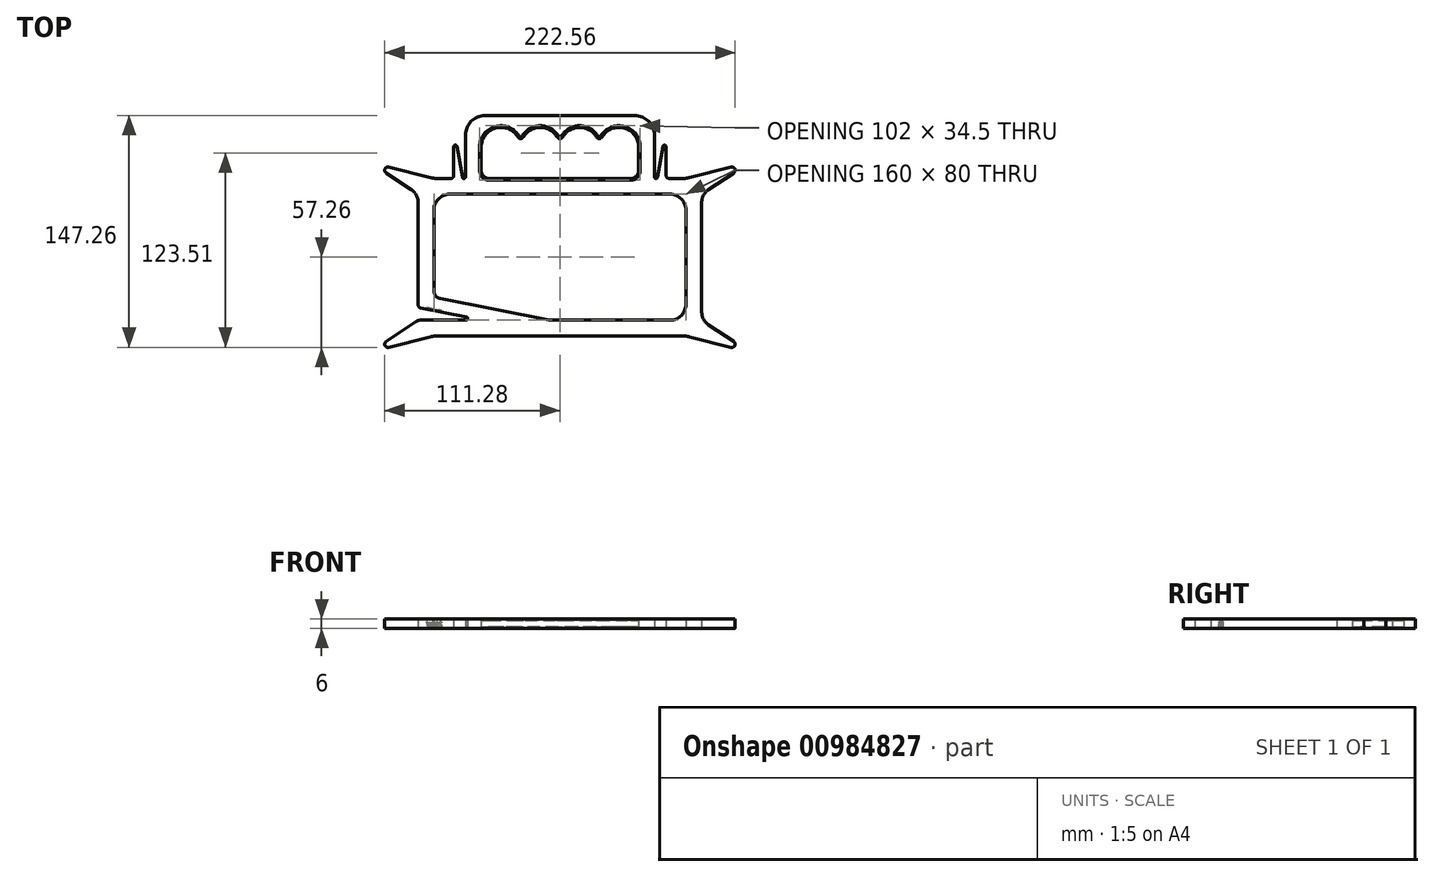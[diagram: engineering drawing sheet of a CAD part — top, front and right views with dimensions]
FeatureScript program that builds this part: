
annotation { "Feature Type Name" : "Feature", "Feature Type Description" : "" }
export const myFeature = defineFeature(function(context is Context, id is Id, definition is map)
    precondition{}
    {
        {
            var Q0;
            Q0=qCreatedBy(makeId("Top.planeOp"),FACE);
            var sketch = newSketch(context, id + "F0", { "sketchPlane" : qUnion([Q0])});
            skLineSegment(sketch, "E0.top", {"start": v(-77.54, -50) * mm, "end": v(77.54, -50) * mm});
            skLineSegment(sketch, "E0.left", {"start": v(-90, 34.65) * mm, "end": v(-90, -30.34) * mm});
            skLineSegment(sketch, "E0.right", {"start": v(90, 34.65) * mm, "end": v(90, -34.65) * mm});
            skLineSegment(sketch, "E1.bottom", {"start": v(70, 40) * mm, "end": v(-70, 40) * mm});
            skLineSegment(sketch, "E1.top", {"start": v(-59.6, -40) * mm, "end": v(-68.78, -40) * mm});
            skLineSegment(sketch, "E1.left", {"start": v(80, 30) * mm, "end": v(80, -30) * mm});
            skLineSegment(sketch, "E1.right", {"start": v(-80, 30) * mm, "end": v(-80, -21.4) * mm});
            skPoint(sketch, "E1.middle", {"position": v(0, 0) * mm});
            skLineSegment(sketch, "E2.top", {"start": v(47.5, 90) * mm, "end": v(-47.5, 90) * mm});
            skLineSegment(sketch, "E2.right", {"start": v(-60, 51) * mm, "end": v(-60, 77.5) * mm});
            skPoint(sketch, "E2.middle", {"position": v(0, 70) * mm});
            skLineSegment(sketch, "E3.top", {"start": v(45, 50) * mm, "end": v(-45, 50) * mm});
            skLineSegment(sketch, "E3.left", {"start": v(50, 70) * mm, "end": v(50, 55) * mm});
            skLineSegment(sketch, "E3.right", {"start": v(-50, 70) * mm, "end": v(-50, 55) * mm});
            skPoint(sketch, "E3.middle", {"position": v(0, 60) * mm});
            skArc(sketch, "E4", {"start": v(-26.72, 76.33) * mm, "mid": v(-40.78, 82.06) * mm, "end": v(-50, 70) * mm});
            skArc(sketch, "E5.1.0.0", {"start": v(-1.72, 76.33) * mm, "mid": v(-12.5, 82.5) * mm, "end": v(-23.28, 76.33) * mm});
            skArc(sketch, "E5.2.0.0", {"start": v(23.28, 76.33) * mm, "mid": v(12.5, 82.5) * mm, "end": v(1.72, 76.33) * mm});
            skArc(sketch, "E5.3.0.0", {"start": v(50, 70) * mm, "mid": v(40.78, 82.06) * mm, "end": v(26.72, 76.33) * mm});
            skPoint(sketch, "E6.visualSharp", {"position": v(-25, 70) * mm});
            skArc(sketch, "E6.filletArc", {"start": v(-26.72, 76.33) * mm, "mid": v(-25, 75.35) * mm, "end": v(-23.28, 76.33) * mm});
            skArc(sketch, "E7.filletArc", {"start": v(-1.72, 76.33) * mm, "mid": v(0, 75.35) * mm, "end": v(1.72, 76.33) * mm});
            skPoint(sketch, "E8.visualSharp", {"position": v(25, 70) * mm});
            skArc(sketch, "E8.filletArc", {"start": v(23.28, 76.33) * mm, "mid": v(25, 75.35) * mm, "end": v(26.72, 76.33) * mm});
            skPoint(sketch, "E9.visualSharp", {"position": v(-60, 90) * mm});
            skArc(sketch, "E9.filletArc", {"start": v(-47.5, 90) * mm, "mid": v(-56.34, 86.34) * mm, "end": v(-60, 77.5) * mm});
            skPoint(sketch, "E10.visualSharp", {"position": v(60, 90) * mm});
            skArc(sketch, "E10.filletArc", {"start": v(60, 77.5) * mm, "mid": v(56.34, 86.34) * mm, "end": v(47.5, 90) * mm});
            skPoint(sketch, "E11.visualSharp", {"position": v(-50, 50) * mm});
            skArc(sketch, "E11.filletArc", {"start": v(-50, 55) * mm, "mid": v(-48.54, 51.46) * mm, "end": v(-45, 50) * mm});
            skPoint(sketch, "E12.visualSharp", {"position": v(50, 50) * mm});
            skArc(sketch, "E12.filletArc", {"start": v(45, 50) * mm, "mid": v(48.54, 51.46) * mm, "end": v(50, 55) * mm});
            skPoint(sketch, "E13.visualSharp", {"position": v(-60, 50) * mm});
            skPoint(sketch, "E14.visualSharp", {"position": v(-80, 40) * mm});
            skPoint(sketch, "E15.visualSharp", {"position": v(-80, -40) * mm});
            skPoint(sketch, "E16.visualSharp", {"position": v(80, -40) * mm});
            skPoint(sketch, "E17.visualSharp", {"position": v(80, 40) * mm});
            skLineSegment(sketch, "E18", {"start": v(94.45, 42.97) * mm, "end": v(110.4, 53.6) * mm});
            skLineSegment(sketch, "E19", {"start": v(82.39, 50.6) * mm, "end": v(108.8, 57.2) * mm});
            skPoint(sketch, "E20.visualSharp", {"position": v(120, 60) * mm});
            skArc(sketch, "E20.filletArc", {"start": v(110.4, 53.6) * mm, "mid": v(111.11, 56.07) * mm, "end": v(108.8, 57.2) * mm});
            skLineSegment(sketch, "E21.MirrorCS", {"start": v(-82.39, 50.6) * mm, "end": v(-108.8, 57.2) * mm});
            skLineSegment(sketch, "E22.MirrorCS", {"start": v(-94.45, 42.97) * mm, "end": v(-110.4, 53.6) * mm});
            skArc(sketch, "E23.MirrorCS", {"start": v(-110.4, 53.6) * mm, "mid": v(-111.11, 56.07) * mm, "end": v(-108.8, 57.2) * mm});
            skLineSegment(sketch, "E24.MirrorCS", {"start": v(-82.39, -50.6) * mm, "end": v(-108.8, -57.2) * mm});
            skArc(sketch, "E25.MirrorCS", {"start": v(-110.4, -53.6) * mm, "mid": v(-111.11, -56.07) * mm, "end": v(-108.8, -57.2) * mm});
            skLineSegment(sketch, "E26.MirrorCS", {"start": v(-91.26, -40.84) * mm, "end": v(-110.4, -53.6) * mm});
            skLineSegment(sketch, "E27.MirrorCS", {"start": v(82.39, -50.6) * mm, "end": v(108.8, -57.2) * mm});
            skLineSegment(sketch, "E28.MirrorCS", {"start": v(94.45, -42.97) * mm, "end": v(110.4, -53.6) * mm});
            skArc(sketch, "E29.MirrorCS", {"start": v(110.4, -53.6) * mm, "mid": v(111.11, -56.07) * mm, "end": v(108.8, -57.2) * mm});
            skPoint(sketch, "E30.visualSharp", {"position": v(90, 40) * mm});
            skArc(sketch, "E30.filletArc", {"start": v(94.45, 42.97) * mm, "mid": v(91.18, 39.37) * mm, "end": v(90, 34.65) * mm});
            skPoint(sketch, "E31.visualSharp", {"position": v(90, -40) * mm});
            skArc(sketch, "E31.filletArc", {"start": v(90, -34.65) * mm, "mid": v(91.18, -39.37) * mm, "end": v(94.45, -42.97) * mm});
            skPoint(sketch, "E32.visualSharp", {"position": v(-90, -40) * mm});
            skPoint(sketch, "E33.visualSharp", {"position": v(-90, 40) * mm});
            skArc(sketch, "E33.filletArc", {"start": v(-90, 34.65) * mm, "mid": v(-91.18, 39.37) * mm, "end": v(-94.45, 42.97) * mm});
            skArc(sketch, "E34.filletArc", {"start": v(-70, 40) * mm, "mid": v(-77.07, 37.07) * mm, "end": v(-80, 30) * mm});
            skArc(sketch, "E35.filletArc", {"start": v(80, 30) * mm, "mid": v(77.07, 37.07) * mm, "end": v(70, 40) * mm});
            skArc(sketch, "E36.filletArc", {"start": v(70, -40) * mm, "mid": v(77.07, -37.07) * mm, "end": v(80, -30) * mm});
            skPoint(sketch, "E37.visualSharp", {"position": v(80, -50) * mm});
            skArc(sketch, "E37.filletArc", {"start": v(82.39, -50.6) * mm, "mid": v(79.98, -50.15) * mm, "end": v(77.54, -50) * mm});
            skPoint(sketch, "E38.visualSharp", {"position": v(-80, -50) * mm});
            skArc(sketch, "E38.filletArc", {"start": v(-77.54, -50) * mm, "mid": v(-79.98, -50.15) * mm, "end": v(-82.39, -50.6) * mm});
            skPoint(sketch, "E39.visualSharp", {"position": v(-80, 50) * mm});
            skArc(sketch, "E39.filletArc", {"start": v(-82.39, 50.6) * mm, "mid": v(-79.98, 50.15) * mm, "end": v(-77.54, 50) * mm});
            skPoint(sketch, "E40.visualSharp", {"position": v(80, 50) * mm});
            skArc(sketch, "E40.filletArc", {"start": v(77.54, 50) * mm, "mid": v(79.98, 50.15) * mm, "end": v(82.39, 50.6) * mm});
            skLineSegment(sketch, "E41", {"start": v(-88.49, -40) * mm, "end": v(-80, -40) * mm});
            skLineSegment(sketch, "E42.bottom", {"start": v(-90, -40) * mm, "end": v(-70.78, -40) * mm});
            skLineSegment(sketch, "E43", {"start": v(-88.39, -32.3) * mm, "end": v(-59.4, -38.02) * mm});
            skPoint(sketch, "E44.orphan", {"position": v(-68.83, -32.33) * mm});
            skArc(sketch, "E45.filletArc", {"start": v(-88.49, -40) * mm, "mid": v(-89.94, -40.21) * mm, "end": v(-91.26, -40.84) * mm});
            skPoint(sketch, "E46.visualSharp", {"position": v(-68.78, -40) * mm});
            skPoint(sketch, "E47.visualSharp", {"position": v(-68.8, -36.16) * mm});
            skArc(sketch, "E48.filletArc", {"start": v(-90, -30.34) * mm, "mid": v(-89.55, -31.6) * mm, "end": v(-88.39, -32.3) * mm});
            skLineSegment(sketch, "E49.0", {"start": v(-58.78, -38) * mm, "end": v(-58.78, -38) * mm});
            skLineSegment(sketch, "E50.trimOffspring", {"start": v(-68.78, -40) * mm, "end": v(-80, -40) * mm});
            skPoint(sketch, "E51.visualSharp", {"position": v(-58.95, -40) * mm});
            skArc(sketch, "E52.filletArc", {"start": v(-59.6, -40) * mm, "mid": v(-58.6, -39.1) * mm, "end": v(-59.4, -38.02) * mm});
            skLineSegment(sketch, "E53", {"start": v(-59.6, -40) * mm, "end": v(-58.95, -40) * mm});
            skLineSegment(sketch, "E54.trimOffspring", {"start": v(-6.06, -40) * mm, "end": v(70, -40) * mm});
            skPoint(sketch, "E55.visualSharp", {"position": v(-48.64, -40) * mm});
            skPoint(sketch, "E56.visualSharp", {"position": v(-80, -25.51) * mm});
            skLineSegment(sketch, "E57", {"start": v(-75.97, -26.3) * mm, "end": v(-7.03, -39.9) * mm});
            skArc(sketch, "E58.filletArc", {"start": v(-80, -21.4) * mm, "mid": v(-78.86, -24.58) * mm, "end": v(-75.97, -26.3) * mm});
            skPoint(sketch, "E59.visualSharp", {"position": v(-6.55, -40) * mm});
            skArc(sketch, "E59.filletArc", {"start": v(-7.03, -39.9) * mm, "mid": v(-6.55, -39.98) * mm, "end": v(-6.06, -40) * mm});
            skLineSegment(sketch, "E60", {"start": v(-69.42, 50) * mm, "end": v(-77.54, 50) * mm});
            skLineSegment(sketch, "E61", {"start": v(-65.43, 70.38) * mm, "end": v(-61.98, 50.83) * mm});
            skArc(sketch, "E62.filletArc", {"start": v(-61.98, 50.83) * mm, "mid": v(-60.91, 50) * mm, "end": v(-60, 51) * mm});
            skLineSegment(sketch, "E63", {"start": v(-67.42, 70.2) * mm, "end": v(-67.42, 52) * mm});
            skArc(sketch, "E64.filletArc", {"start": v(-69.42, 50) * mm, "mid": v(-68, 50.59) * mm, "end": v(-67.42, 52) * mm});
            skPoint(sketch, "E65.newPointA", {"position": v(-66.24, 74.98) * mm});
            skPoint(sketch, "E65.newPointB", {"position": v(-67.42, 74.98) * mm});
            skArc(sketch, "E65.filletArc", {"start": v(-65.43, 70.38) * mm, "mid": v(-66.5, 71.2) * mm, "end": v(-67.42, 70.2) * mm});
            skArc(sketch, "E66.MirrorCS", {"start": v(65.43, 70.38) * mm, "mid": v(66.5, 71.2) * mm, "end": v(67.42, 70.2) * mm});
            skArc(sketch, "E67.MirrorCS", {"start": v(69.42, 50) * mm, "mid": v(68, 50.59) * mm, "end": v(67.42, 52) * mm});
            skArc(sketch, "E68.MirrorCS", {"start": v(61.98, 50.83) * mm, "mid": v(60.91, 50) * mm, "end": v(60, 51) * mm});
            skPoint(sketch, "E69.MirrorP", {"position": v(60, 50) * mm});
            skLineSegment(sketch, "E70.MirrorCS", {"start": v(60, 51) * mm, "end": v(60, 77.5) * mm});
            skLineSegment(sketch, "E71.MirrorCS", {"start": v(69.42, 50) * mm, "end": v(77.54, 50) * mm});
            skPoint(sketch, "E72.MirrorP", {"position": v(66.24, 74.98) * mm});
            skPoint(sketch, "E73.MirrorP", {"position": v(67.42, 74.98) * mm});
            skLineSegment(sketch, "E74.MirrorCS", {"start": v(67.42, 70.2) * mm, "end": v(67.42, 52) * mm});
            skLineSegment(sketch, "E75.MirrorCS", {"start": v(65.43, 70.38) * mm, "end": v(61.98, 50.83) * mm});
            skSolve(sketch);
        }
        {
            var Q0;
            Q0=makeQuery(id+"F0.imprint","IMPRINT",FACE,{"disambiguationData":[TD([[makeQuery(id+"F0.imprint","IMPRINT",EDGE,{"derivedFrom":sQuery(id+"F0.wireOp",EDGE,"E0.bottom")}),-1.0]])]});
            var Q1;
            Q1=makeQuery(id+"F0.imprint","IMPRINT",FACE,{"disambiguationData":[TD([[makeQuery(id+"F0.imprint","IMPRINT",EDGE,{"derivedFrom":sQuery(id+"F0.wireOp",EDGE,"E0.top")}),1.0]])]});
            extrude(context, id + "F1", {"entities" : qUnion([Q0, Q1]), "depth" : 6 * mm, "offsetDistance" : 25 * mm});
        }
        {
            var Q0;
            Q0=makeQuery(id+"F1.opExtrude","CAP_EDGE",EDGE,{"disambiguationData":[OSD([sQuery(id+"F0.wireOp",EDGE,"E3.right")])],"isStart":false});
            var Q1;
            Q1=makeQuery(id+"F1.opExtrude","CAP_EDGE",EDGE,{"disambiguationData":[OSD([sQuery(id+"F0.wireOp",EDGE,"E4")])],"isStart":false});
            var Q2;
            Q2=makeQuery(id+"F1.opExtrude","CAP_EDGE",EDGE,{"disambiguationData":[OSD([sQuery(id+"F0.wireOp",EDGE,"E6.filletArc")])],"isStart":false});
            chamfer(context, id + "F2", {"entities" : qUnion([Q0, Q1, Q2]), "width" : 1 * mm, "tangentPropagation" : true});
        }
        {
            var Q0;
            Q0=makeQuery(id+"F1.opExtrude","CAP_EDGE",EDGE,{"disambiguationData":[OSD([sQuery(id+"F0.wireOp",EDGE,"E5.3.0.0")])],"isStart":true});
            var Q1;
            Q1=makeQuery(id+"F1.opExtrude","CAP_EDGE",EDGE,{"disambiguationData":[OSD([sQuery(id+"F0.wireOp",EDGE,"E8.filletArc")])],"isStart":true});
            var Q2;
            Q2=makeQuery(id+"F1.opExtrude","CAP_EDGE",EDGE,{"disambiguationData":[OSD([sQuery(id+"F0.wireOp",EDGE,"E3.left")])],"isStart":true});
            var Q3;
            Q3=makeQuery(id+"F1.opExtrude","CAP_EDGE",EDGE,{"disambiguationData":[OSD([sQuery(id+"F0.wireOp",EDGE,"E3.top")])],"isStart":true});
            var Q4;
            Q4=makeQuery(id+"F1.opExtrude","CAP_EDGE",EDGE,{"disambiguationData":[OSD([sQuery(id+"F0.wireOp",EDGE,"E12.filletArc")])],"isStart":true});
            chamfer(context, id + "F3", {"entities" : qUnion([Q0, Q1, Q2, Q3, Q4]), "width" : 1 * mm, "tangentPropagation" : true});
        }
        {
            var Q0;
            Q0=makeQuery(id+"F1.opExtrude","SWEPT_FACE",FACE,{"disambiguationData":[OSD([sQuery(id+"F0.wireOp",EDGE,"E43")])]});
            var sketch = newSketch(context, id + "F4", { "sketchPlane" : qUnion([Q0])});
            skText(sketch, "E76", { "text": "WHS", "fontName": "OpenSans-Regular.ttf"});
            const initialGuessF4  = {"E76": [-0.07674, 0.0009, 1, 0, 0.0032]};
            skSetInitialGuess(sketch, initialGuessF4);
            skSolve(sketch);
        }
        {
            var Q0;
            Q0 = qSketchRegion(id + "F4", true);
            extrude(context, id + "F5", {"entities" : qUnion([Q0]), "operationType" : NewBodyOperationType.REMOVE, "oppositeDirection" : true, "depth" : 1 * mm, "offsetDistance" : 25 * mm});
        }
    });
